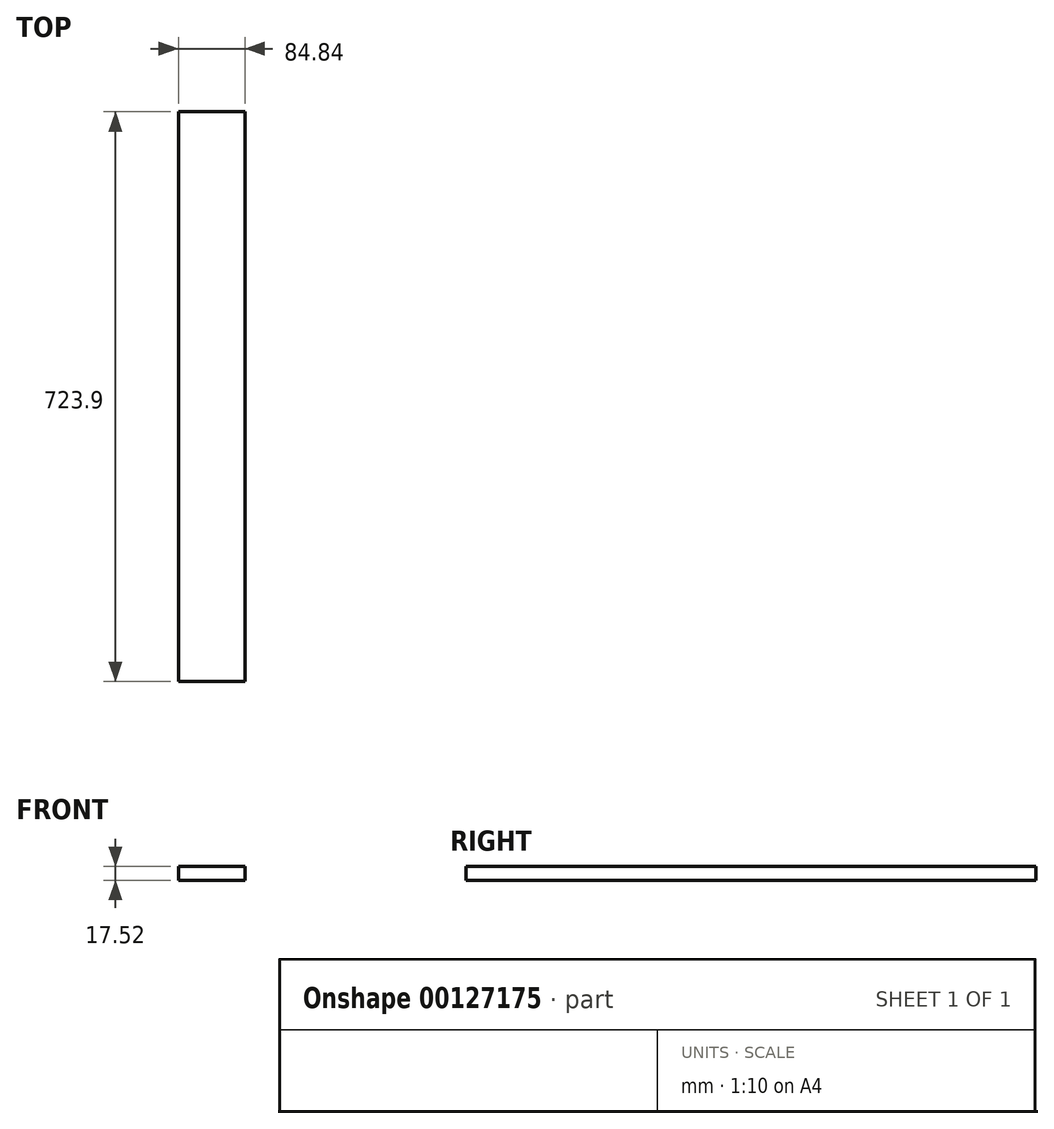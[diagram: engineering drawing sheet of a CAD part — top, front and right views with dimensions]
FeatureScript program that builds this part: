
annotation { "Feature Type Name" : "Feature", "Feature Type Description" : "" }
export const myFeature = defineFeature(function(context is Context, id is Id, definition is map)
    precondition{}
    {
        {
            var Q0;
            Q0=qCreatedBy(makeId("Front.planeOp"),FACE);
            var sketch = newSketch(context, id + "F0", { "sketchPlane" : qUnion([Q0])});
            skLineSegment(sketch, "E0.bottom", {"start": v(42.42, -8.76) * mm, "end": v(-42.42, -8.76) * mm});
            skLineSegment(sketch, "E0.top", {"start": v(42.42, 8.76) * mm, "end": v(-42.42, 8.76) * mm});
            skLineSegment(sketch, "E0.left", {"start": v(42.42, -8.76) * mm, "end": v(42.42, 8.76) * mm});
            skLineSegment(sketch, "E0.right", {"start": v(-42.42, -8.76) * mm, "end": v(-42.42, 8.76) * mm});
            skPoint(sketch, "E0.middle", {"position": v(0, 0) * mm});
            skSolve(sketch);
        }
        {
            var Q0;
            Q0=qSketchRegion(id+"F0",true);
            extrude(context, id + "F1", {"entities" : qUnion([Q0]), "depth" : 723.9 * mm, "offsetDistance" : 25.4 * mm});
        }
    });
